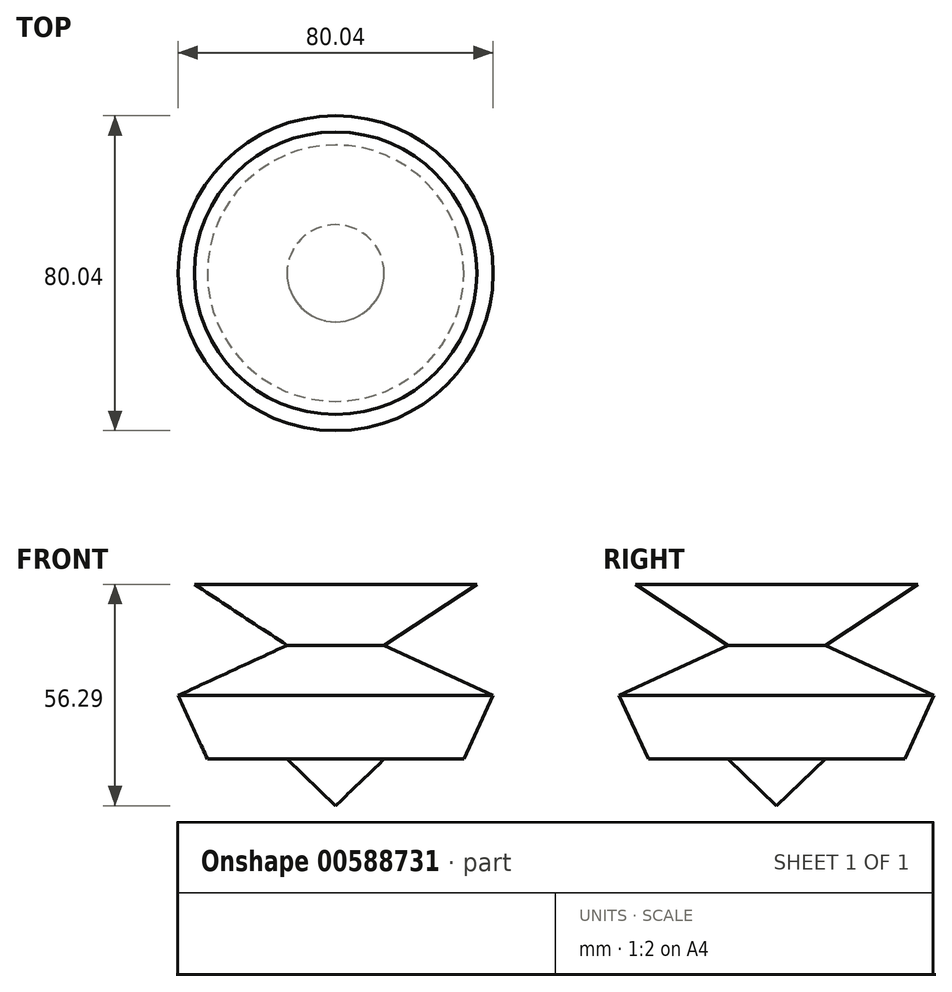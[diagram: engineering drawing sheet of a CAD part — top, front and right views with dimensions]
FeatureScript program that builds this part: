
annotation { "Feature Type Name" : "Feature", "Feature Type Description" : "" }
export const myFeature = defineFeature(function(context is Context, id is Id, definition is map)
    precondition{}
    {
        {
            var Q0;
            Q0=qCreatedBy(makeId("Right.planeOp"),FACE);
            var sketch = newSketch(context, id + "F0", { "sketchPlane" : qUnion([Q0])});
            skLineSegment(sketch, "E0", {"start": v(0, 56.29) * mm, "end": v(-35.89, 56.29) * mm});
            skLineSegment(sketch, "E1", {"start": v(-35.89, 56.29) * mm, "end": v(-12.34, 40.78) * mm});
            skLineSegment(sketch, "E2", {"start": v(-12.34, 40.78) * mm, "end": v(-40.02, 28.01) * mm});
            skLineSegment(sketch, "E3", {"start": v(-40.02, 28.01) * mm, "end": v(-32.56, 11.87) * mm});
            skLineSegment(sketch, "E4", {"start": v(-32.56, 11.87) * mm, "end": v(-12.34, 11.87) * mm});
            skLineSegment(sketch, "E5", {"start": v(-12.34, 11.87) * mm, "end": v(0, 0) * mm});
            skLineSegment(sketch, "E6", {"start": v(0, 0) * mm, "end": v(0, 56.29) * mm});
            skSolve(sketch);
        }
        {
            var Q0;
            Q0=makeQuery(id+"F0.imprint","IMPRINT",FACE,{"disambiguationData":[TD([[makeQuery(id+"F0.imprint","IMPRINT",EDGE,{"derivedFrom":sQuery(id+"F0.wireOp",EDGE,"E0")}),1.0]])]});
            var Q1;
            Q1=sQuery(id+"F0.wireOp",EDGE,"E6");
            revolve(context, id + "F1", {"entities" : qUnion([Q0]), "axis" : qUnion([Q1]), "revolveType" : RevolveType.FULL});
        }
    });
